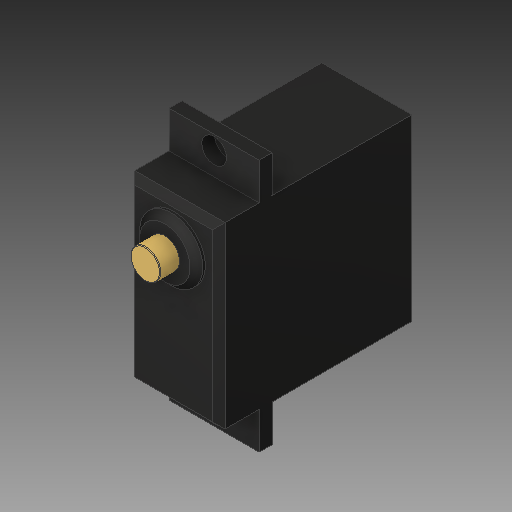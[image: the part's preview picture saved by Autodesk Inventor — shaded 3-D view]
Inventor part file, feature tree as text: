
AUTODESK INVENTOR PART (.ipt)
format: ipt  version: 2018.1 (Build 221171000, 171)  size: 154,112 bytes
history: native  units: mm
features: other x1, extrude x1, sketch x1, imported_body x1
ambient origin geometry x8: Origin, YZ Plane, XZ Plane, XY Plane, X Axis, Y Axis, Z Axis, Center Point
bodies: Body1 (feature_tree)
feature tree (4):
  other  "ソリッド1"
  extrude  "押し出し1"  Depth=10.0mm TaperAngle=0.0deg
  sketch  "スケッチ1"
  imported_body  "Base1"
